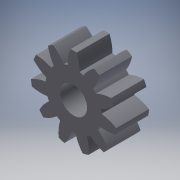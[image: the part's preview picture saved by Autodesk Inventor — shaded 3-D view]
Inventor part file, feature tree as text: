
AUTODESK INVENTOR PART (.ipt)
format: ipt  version: 2016 (Build 200138000, 138)  size: 193,536 bytes
history: native  units: mm (DEFAULTED — no unit token found)
features: plane x3, other x3, sketch x2, extrude x1, hole x1
ambient origin geometry x8: Origin, YZ Plane, XZ Plane, XY Plane, X Axis, Y Axis, Z Axis, Center Point
bodies: Solid1 (feature_tree)
feature tree (10):
  extrude  "Extrusion1"  Depth=6.35mm TaperAngle=0.0deg
  plane  "Work Plane1"
  plane  "Work Plane2"
  plane  "Work Plane3"
  other  "Spur Gear"
  hole  "Hole1"  [1 undecoded]
  sketch  "Sketch1"  dims[d0=16.51mm d1=6.35mm d2=0.0mm]
  sketch  "Sketch2"  dims[d3=13.97mm d4=76.2mm d5=0.0mm d6=0.0mm d7=2.855993mm d9=0.0mm d14=0.0mm d15=41.91mm d16=0.0mm d17=0.0mm d18=0.0mm d19=41.91mm d29=25.4mm d30=25.4mm d22=5.207mm d23=19.05mm d24=9.525mm d25=6.35mm d26=14.3117mm d27=25.4mm d28=20.594885mm]
  other  "Srf1"
  other  "Pitch Diameter"
note: 1 required parameter value undecoded (feature->parameter linkage not recoverable at this tier; creation-order binding heuristic only, values carry confidence <= 0.55)
